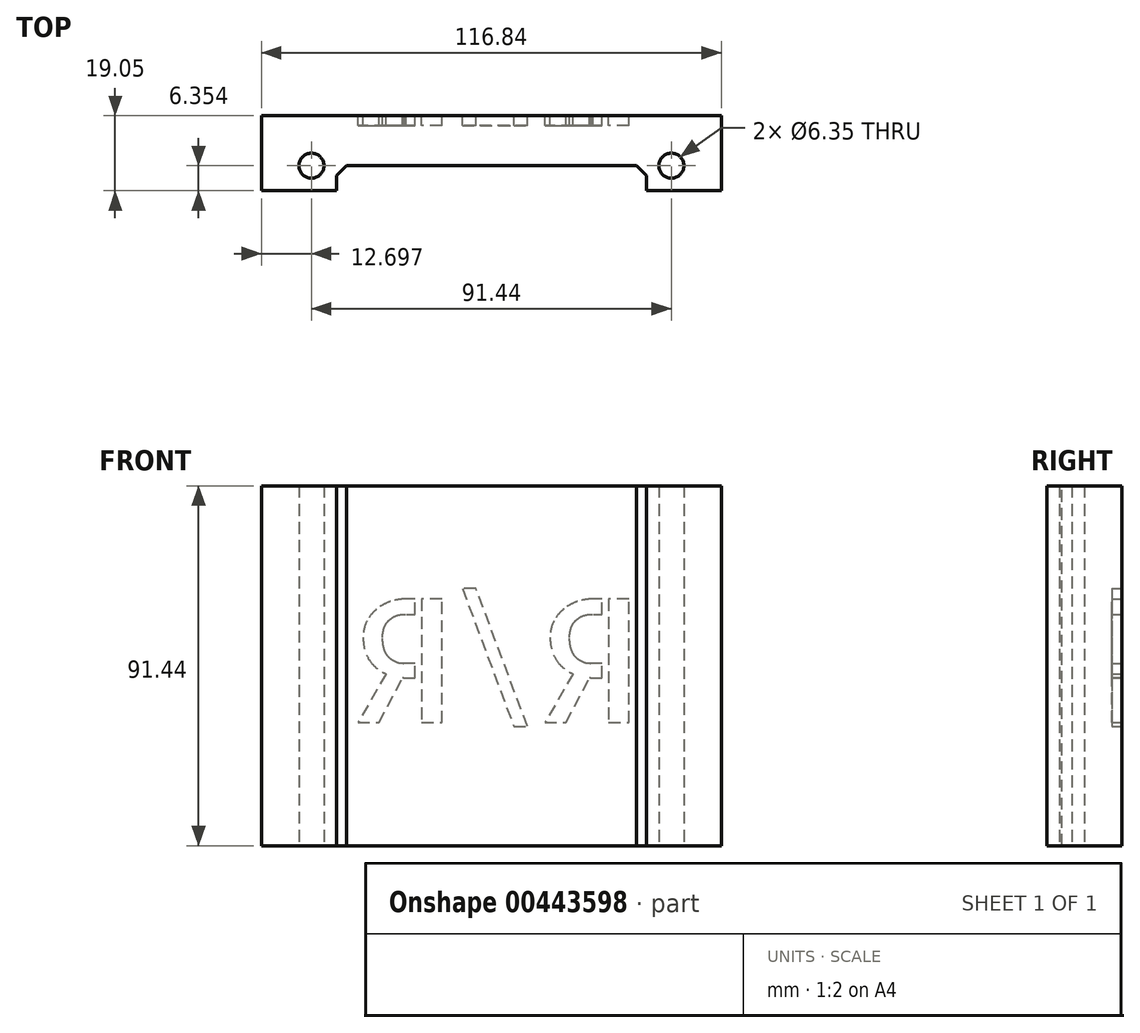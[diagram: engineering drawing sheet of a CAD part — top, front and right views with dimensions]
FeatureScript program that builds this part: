
annotation { "Feature Type Name" : "Feature", "Feature Type Description" : "" }
export const myFeature = defineFeature(function(context is Context, id is Id, definition is map)
    precondition{}
    {
        {
            var Q0;
            Q0=qCreatedBy(makeId("Top.planeOp"),FACE);
            var sketch = newSketch(context, id + "F0", { "sketchPlane" : qUnion([Q0])});
            skLineSegment(sketch, "E0.bottom", {"start": v(-65.86, 39.92) * mm, "end": v(50.98, 39.92) * mm});
            skLineSegment(sketch, "E0.top", {"start": v(-65.86, 27.22) * mm, "end": v(50.98, 27.22) * mm});
            skLineSegment(sketch, "E0.left", {"start": v(-65.86, 39.92) * mm, "end": v(-65.86, 27.22) * mm});
            skLineSegment(sketch, "E0.right", {"start": v(50.98, 39.92) * mm, "end": v(50.98, 27.22) * mm});
            skLineSegment(sketch, "E1.top", {"start": v(-65.86, 20.87) * mm, "end": v(-46.81, 20.87) * mm});
            skLineSegment(sketch, "E1.left", {"start": v(-65.86, 27.22) * mm, "end": v(-65.86, 20.87) * mm});
            skLineSegment(sketch, "E1.right", {"start": v(-46.81, 27.22) * mm, "end": v(-46.81, 20.87) * mm});
            skLineSegment(sketch, "E2.top", {"start": v(50.98, 20.87) * mm, "end": v(31.93, 20.87) * mm});
            skLineSegment(sketch, "E2.left", {"start": v(50.98, 27.22) * mm, "end": v(50.98, 20.87) * mm});
            skLineSegment(sketch, "E2.right", {"start": v(31.93, 27.22) * mm, "end": v(31.93, 20.87) * mm});
            skCircle(sketch, "E3", {"center": v(-53.16, 27.22) * mm, "radius": 3.18 * mm});
            skCircle(sketch, "E4", {"center": v(38.28, 27.22) * mm, "radius": 3.18 * mm});
            skLineSegment(sketch, "E5", {"start": v(-65.86, 27.22) * mm, "end": v(-53.16, 27.22) * mm});
            skLineSegment(sketch, "E6", {"start": v(38.28, 27.22) * mm, "end": v(50.98, 27.22) * mm});
            skSolve(sketch);
        }
        {
            var Q0;
            Q0 = qSketchRegion(id + "F0", true);
            extrude(context, id + "F1", {"entities" : qUnion([Q0]), "depth" : 91.44 * mm});
        }
        {
            var Q0;
            Q0=makeQuery(id+"F1.opExtrude","SWEPT_EDGE",EDGE,{"disambiguationData":[OSD([sQuery(id+"F0.wireOp",EDGE,"E0.top"),sQuery(id+"F0.wireOp",EDGE,"E1.right")])]});
            var Q1;
            Q1=makeQuery(id+"F1.opExtrude","SWEPT_EDGE",EDGE,{"disambiguationData":[OSD([sQuery(id+"F0.wireOp",EDGE,"E0.top"),sQuery(id+"F0.wireOp",EDGE,"E2.right")])]});
            chamfer(context, id + "F2", {"entities" : qUnion([Q0, Q1]), "width" : 2.54 * mm, "tangentPropagation" : true});
        }
        {
            var Q0;
            Q0=makeQuery(id+"F1.opExtrude","SWEPT_FACE",FACE,{"disambiguationData":[OSD([sQuery(id+"F0.wireOp",EDGE,"E0.bottom")])]});
            var sketch = newSketch(context, id + "F3", { "sketchPlane" : qUnion([Q0])});
            skText(sketch, "E7", { "text": "R/R", "fontName": "AllertaStencil-Regular.ttf"});
            const initialGuessF3  = {"E7": [-0.03132, 0.03129, 1, 0, 0.03144]};
            skSetInitialGuess(sketch, initialGuessF3);
            skSolve(sketch);
        }
        {
            var Q0;
            Q0 = qSketchRegion(id + "F3", true);
            extrude(context, id + "F4", {"entities" : qUnion([Q0]), "operationType" : NewBodyOperationType.REMOVE, "oppositeDirection" : true, "depth" : 2.54 * mm});
        }
    });
